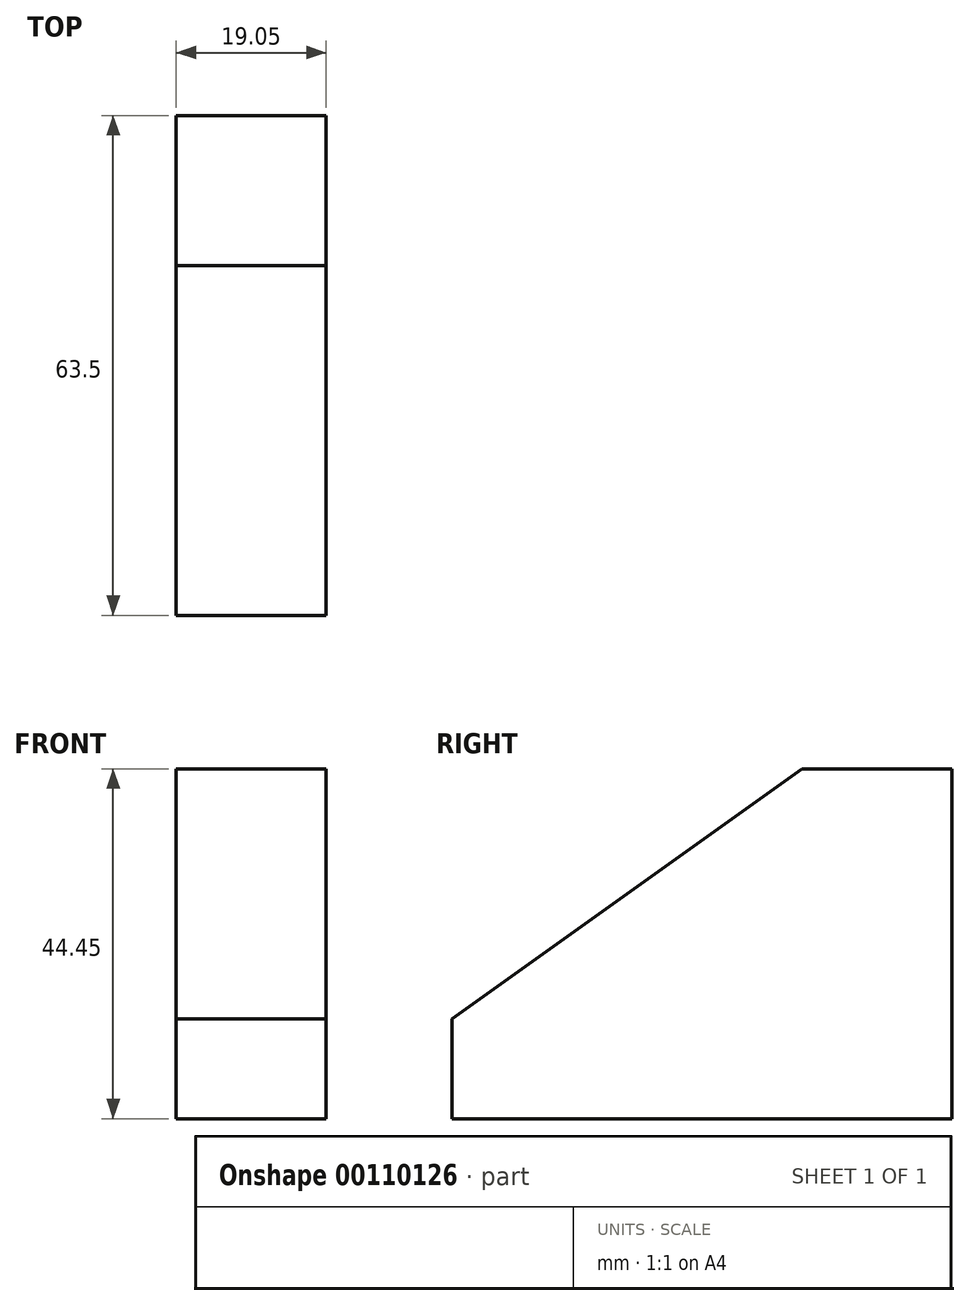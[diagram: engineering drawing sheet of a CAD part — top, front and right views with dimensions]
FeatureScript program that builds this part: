
annotation { "Feature Type Name" : "Feature", "Feature Type Description" : "" }
export const myFeature = defineFeature(function(context is Context, id is Id, definition is map)
    precondition{}
    {
        {
            var Q0;
            Q0=qCreatedBy(makeId("Right.planeOp"),FACE);
            var sketch = newSketch(context, id + "F0", { "sketchPlane" : qUnion([Q0])});
            skLineSegment(sketch, "E0", {"start": v(-30.42, -17.51) * mm, "end": v(33.08, -17.51) * mm});
            skLineSegment(sketch, "E1", {"start": v(33.08, -17.51) * mm, "end": v(33.08, 26.94) * mm});
            skLineSegment(sketch, "E2", {"start": v(33.08, 26.94) * mm, "end": v(14.03, 26.94) * mm});
            skLineSegment(sketch, "E3", {"start": v(14.03, 26.94) * mm, "end": v(-30.42, -4.81) * mm});
            skLineSegment(sketch, "E4", {"start": v(-30.42, -4.81) * mm, "end": v(-30.42, -17.51) * mm});
            skSolve(sketch);
        }
        {
            var Q0;
            Q0=makeQuery(id+"F0.imprint","IMPRINT",FACE,{"disambiguationData":[TD([[makeQuery(id+"F0.imprint","IMPRINT",EDGE,{"derivedFrom":sQuery(id+"F0.wireOp",EDGE,"E0")}),1.0]])]});
            extrude(context, id + "F1", {"entities" : qUnion([Q0]), "oppositeDirection" : true, "depth" : 19.05 * mm});
        }
    });
